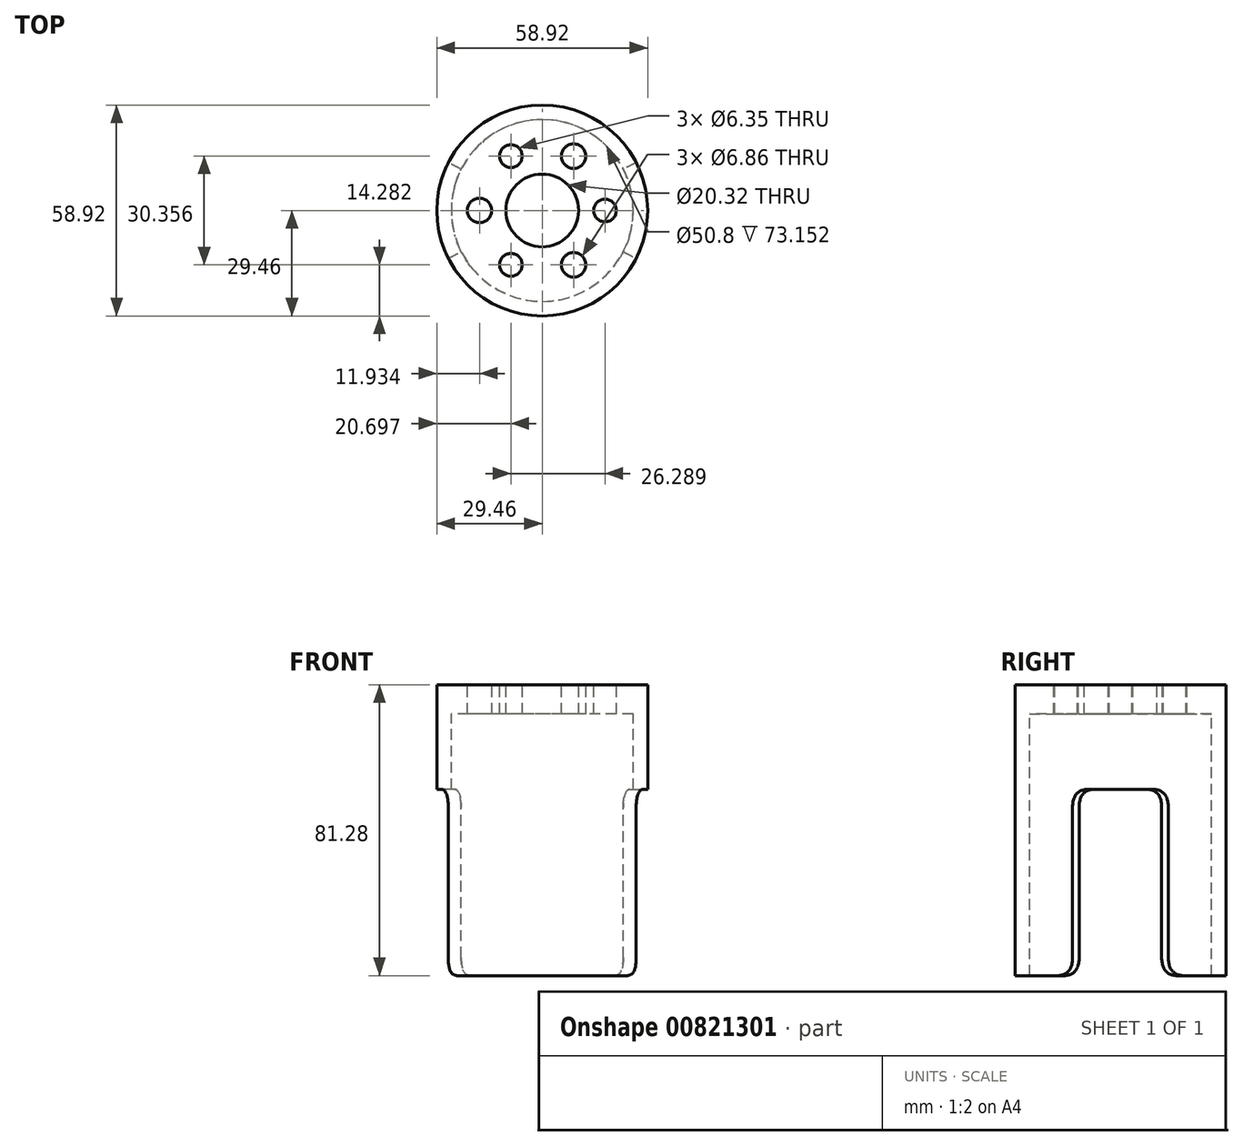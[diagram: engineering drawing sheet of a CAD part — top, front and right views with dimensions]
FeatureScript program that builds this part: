
annotation { "Feature Type Name" : "Feature", "Feature Type Description" : "" }
export const myFeature = defineFeature(function(context is Context, id is Id, definition is map)
    precondition{}
    {
        {
            var Q0;
            Q0=qCreatedBy(makeId("Top.planeOp"),FACE);
            var sketch = newSketch(context, id + "F0", { "sketchPlane" : qUnion([Q0])});
            skCircle(sketch, "E0", {"center": v(0, 0) * mm, "radius": 17.53 * mm, "construction": true});
            skCircle(sketch, "E1", {"center": v(0, 0) * mm, "radius": 10.16 * mm});
            skCircle(sketch, "E2", {"center": v(0, 0) * mm, "radius": 29.46 * mm});
            skCircle(sketch, "E3", {"center": v(17.53, 0) * mm, "radius": 3.18 * mm});
            skCircle(sketch, "E4", {"center": v(-17.53, 0) * mm, "radius": 3.43 * mm});
            skCircle(sketch, "E5.1.0", {"center": v(-8.76, 15.18) * mm, "radius": 3.18 * mm});
            skCircle(sketch, "E5.2.0", {"center": v(-8.76, -15.18) * mm, "radius": 3.18 * mm});
            skCircle(sketch, "E6.1.0", {"center": v(8.76, -15.18) * mm, "radius": 3.43 * mm});
            skCircle(sketch, "E6.2.0", {"center": v(8.76, 15.18) * mm, "radius": 3.43 * mm});
            skSolve(sketch);
        }
        {
            var Q0;
            Q0=makeQuery(id+"F0.imprint","IMPRINT",FACE,{"disambiguationData":[TD([[makeQuery(id+"F0.imprint","IMPRINT",EDGE,{"derivedFrom":sQuery(id+"F0.wireOp",EDGE,"E1")}),-1.0]])]});
            extrude(context, id + "F1", {"entities" : qUnion([Q0]), "oppositeDirection" : true, "depth" : 81.28 * mm, "offsetDistance" : 25.4 * mm});
        }
        {
            var Q0;
            Q0=qCreatedBy(makeId("Top.planeOp"),FACE);
            cPlane(context, id + "F2", {"entities" : qUnion([Q0]), "cplaneType" : CPlaneType.OFFSET, "offset" : 8.13 * mm, "oppositeDirection" : true, "width" : 152.4 * mm, "height" : 152.4 * mm});
        }
        {
            var Q0;
            Q0=qCreatedBy(id+"F2.planeOp",FACE);
            var sketch = newSketch(context, id + "F3", { "sketchPlane" : qUnion([Q0])});
            skCircle(sketch, "E7", {"center": v(0, 0) * mm, "radius": 25.4 * mm});
            skSolve(sketch);
        }
        {
            var Q0;
            Q0=makeQuery(id+"F3.imprint","IMPRINT",FACE,{"disambiguationData":[TD([[makeQuery(id+"F3.imprint","IMPRINT",EDGE,{"derivedFrom":sQuery(id+"F3.wireOp",EDGE,"E7")}),1.0]])]});
            extrude(context, id + "F4", {"entities" : qUnion([Q0]), "operationType" : NewBodyOperationType.REMOVE, "endBound" : BoundingType.THROUGH_ALL, "oppositeDirection" : true, "depth" : 25.4 * mm, "offsetDistance" : 25.4 * mm});
        }
        {
            var Q0;
            Q0=qCreatedBy(makeId("Top.planeOp"),FACE);
            cPlane(context, id + "F5", {"entities" : qUnion([Q0]), "cplaneType" : CPlaneType.OFFSET, "offset" : 29.2 * mm, "oppositeDirection" : true, "width" : 152.4 * mm, "height" : 152.4 * mm});
        }
        {
            var Q0;
            Q0=qCreatedBy(id+"F5.planeOp",FACE);
            var sketch = newSketch(context, id + "F6", { "sketchPlane" : qUnion([Q0])});
            skCircle(sketch, "E8", {"center": v(0, 0) * mm, "radius": 29.46 * mm, "construction": true});
            skCircle(sketch, "E9", {"center": v(0, 0) * mm, "radius": 25.4 * mm, "construction": true});
            skPoint(sketch, "E10", {"position": v(-22.63, 11.53) * mm});
            skPoint(sketch, "E11", {"position": v(-22.63, -11.53) * mm});
            skLineSegment(sketch, "E12", {"start": v(-26.25, 13.38) * mm, "end": v(26.25, -13.38) * mm, "construction": true});
            skLineSegment(sketch, "E13", {"start": v(26.25, 13.38) * mm, "end": v(-26.25, -13.38) * mm, "construction": true});
            skLineSegment(sketch, "E14", {"start": v(-22.63, 11.53) * mm, "end": v(-22.63, -11.53) * mm});
            skLineSegment(sketch, "E15", {"start": v(-22.63, 11.53) * mm, "end": v(-26.25, 13.38) * mm});
            skLineSegment(sketch, "E16", {"start": v(-22.63, -11.53) * mm, "end": v(-26.25, -13.38) * mm});
            skPoint(sketch, "E17", {"position": v(-29.46, 0) * mm});
            skArc(sketch, "E18", {"start": v(-26.25, 13.38) * mm, "mid": v(-29.46, 0) * mm, "end": v(-26.25, -13.38) * mm});
            skPoint(sketch, "E19", {"position": v(22.63, 11.53) * mm});
            skPoint(sketch, "E20", {"position": v(22.63, -11.53) * mm});
            skLineSegment(sketch, "E21", {"start": v(26.25, 13.38) * mm, "end": v(22.63, 11.53) * mm});
            skLineSegment(sketch, "E22", {"start": v(22.63, 11.53) * mm, "end": v(22.63, -11.53) * mm});
            skLineSegment(sketch, "E23", {"start": v(22.63, -11.53) * mm, "end": v(26.25, -13.38) * mm});
            skPoint(sketch, "E24", {"position": v(29.46, 0) * mm});
            skArc(sketch, "E25", {"start": v(26.25, -13.38) * mm, "mid": v(29.46, 0) * mm, "end": v(26.25, 13.38) * mm});
            skSolve(sketch);
        }
        {
            var Q0;
            Q0=qSketchRegion(id+"F6",true);
            extrude(context, id + "F7", {"entities" : qUnion([Q0]), "operationType" : NewBodyOperationType.REMOVE, "endBound" : BoundingType.THROUGH_ALL, "oppositeDirection" : true, "depth" : 25.4 * mm, "offsetDistance" : 25.4 * mm});
        }
        {
            var Q0;
            Q0=makeQuery(id+"F7.boolean.opBoolean","INTERSECT",EDGE,{"derivedFrom":[makeQuery(id+"F1.opExtrude","CAP_FACE",FACE,{"disambiguationData":[OSD([sQuery(id+"F0.wireOp",EDGE,"E1"),sQuery(id+"F0.wireOp",EDGE,"E2"),sQuery(id+"F0.wireOp",EDGE,"E3"),sQuery(id+"F0.wireOp",EDGE,"E4"),sQuery(id+"F0.wireOp",EDGE,"E5.1.0"),sQuery(id+"F0.wireOp",EDGE,"E5.2.0"),sQuery(id+"F0.wireOp",EDGE,"E6.1.0"),sQuery(id+"F0.wireOp",EDGE,"E6.2.0")])],"isStart":false}),makeQuery(id+"F7.opExtrude","SWEPT_FACE",FACE,{"disambiguationData":[OSD([sQuery(id+"F6.wireOp",EDGE,"E23")])]})]});
            var Q1;
            Q1=makeQuery(id+"F7.boolean.opBoolean","INTERSECT",EDGE,{"derivedFrom":[makeQuery(id+"F1.opExtrude","CAP_FACE",FACE,{"disambiguationData":[OSD([sQuery(id+"F0.wireOp",EDGE,"E1"),sQuery(id+"F0.wireOp",EDGE,"E2"),sQuery(id+"F0.wireOp",EDGE,"E3"),sQuery(id+"F0.wireOp",EDGE,"E4"),sQuery(id+"F0.wireOp",EDGE,"E5.1.0"),sQuery(id+"F0.wireOp",EDGE,"E5.2.0"),sQuery(id+"F0.wireOp",EDGE,"E6.1.0"),sQuery(id+"F0.wireOp",EDGE,"E6.2.0")])],"isStart":false}),makeQuery(id+"F7.opExtrude","SWEPT_FACE",FACE,{"disambiguationData":[OSD([sQuery(id+"F6.wireOp",EDGE,"E21")])]})]});
            var Q2;
            Q2=makeQuery(id+"F7.boolean.opBoolean","INTERSECT",EDGE,{"derivedFrom":[makeQuery(id+"F1.opExtrude","CAP_FACE",FACE,{"disambiguationData":[OSD([sQuery(id+"F0.wireOp",EDGE,"E1"),sQuery(id+"F0.wireOp",EDGE,"E2"),sQuery(id+"F0.wireOp",EDGE,"E3"),sQuery(id+"F0.wireOp",EDGE,"E4"),sQuery(id+"F0.wireOp",EDGE,"E5.1.0"),sQuery(id+"F0.wireOp",EDGE,"E5.2.0"),sQuery(id+"F0.wireOp",EDGE,"E6.1.0"),sQuery(id+"F0.wireOp",EDGE,"E6.2.0")])],"isStart":false}),makeQuery(id+"F7.opExtrude","SWEPT_FACE",FACE,{"disambiguationData":[OSD([sQuery(id+"F6.wireOp",EDGE,"E15")])]})]});
            var Q3;
            Q3=makeQuery(id+"F7.boolean.opBoolean","INTERSECT",EDGE,{"derivedFrom":[makeQuery(id+"F1.opExtrude","CAP_FACE",FACE,{"disambiguationData":[OSD([sQuery(id+"F0.wireOp",EDGE,"E1"),sQuery(id+"F0.wireOp",EDGE,"E2"),sQuery(id+"F0.wireOp",EDGE,"E3"),sQuery(id+"F0.wireOp",EDGE,"E4"),sQuery(id+"F0.wireOp",EDGE,"E5.1.0"),sQuery(id+"F0.wireOp",EDGE,"E5.2.0"),sQuery(id+"F0.wireOp",EDGE,"E6.1.0"),sQuery(id+"F0.wireOp",EDGE,"E6.2.0")])],"isStart":false}),makeQuery(id+"F7.opExtrude","SWEPT_FACE",FACE,{"disambiguationData":[OSD([sQuery(id+"F6.wireOp",EDGE,"E16")])]})]});
            fillet(context, id + "F8", {"entities" : qUnion([Q0, Q1, Q2, Q3]), "radius" : 5.08 * mm, "tangentPropagation" : true, "rho" : 0.5, "crossSection" : FilletCrossSection.CONIC, "allowEdgeOverflow" : false});
        }
        {
            var Q0;
            Q0=makeQuery(id+"F7.boolean.opBoolean","COPY",EDGE,{"derivedFrom":makeQuery(id+"F7.opExtrude","CAP_EDGE",EDGE,{"disambiguationData":[OSD([sQuery(id+"F6.wireOp",EDGE,"E16")])],"isStart":true})});
            var Q1;
            Q1=makeQuery(id+"F7.boolean.opBoolean","COPY",EDGE,{"derivedFrom":makeQuery(id+"F7.opExtrude","CAP_EDGE",EDGE,{"disambiguationData":[OSD([sQuery(id+"F6.wireOp",EDGE,"E15")])],"isStart":true})});
            var Q2;
            Q2=makeQuery(id+"F7.boolean.opBoolean","COPY",EDGE,{"derivedFrom":makeQuery(id+"F7.opExtrude","CAP_EDGE",EDGE,{"disambiguationData":[OSD([sQuery(id+"F6.wireOp",EDGE,"E23")])],"isStart":true})});
            var Q3;
            Q3=makeQuery(id+"F7.boolean.opBoolean","COPY",EDGE,{"derivedFrom":makeQuery(id+"F7.opExtrude","CAP_EDGE",EDGE,{"disambiguationData":[OSD([sQuery(id+"F6.wireOp",EDGE,"E21")])],"isStart":true})});
            fillet(context, id + "F9", {"entities" : qUnion([Q0, Q1, Q2, Q3]), "radius" : 5.08 * mm, "tangentPropagation" : true, "rho" : 0.5, "crossSection" : FilletCrossSection.CONIC, "allowEdgeOverflow" : false});
        }
    });
